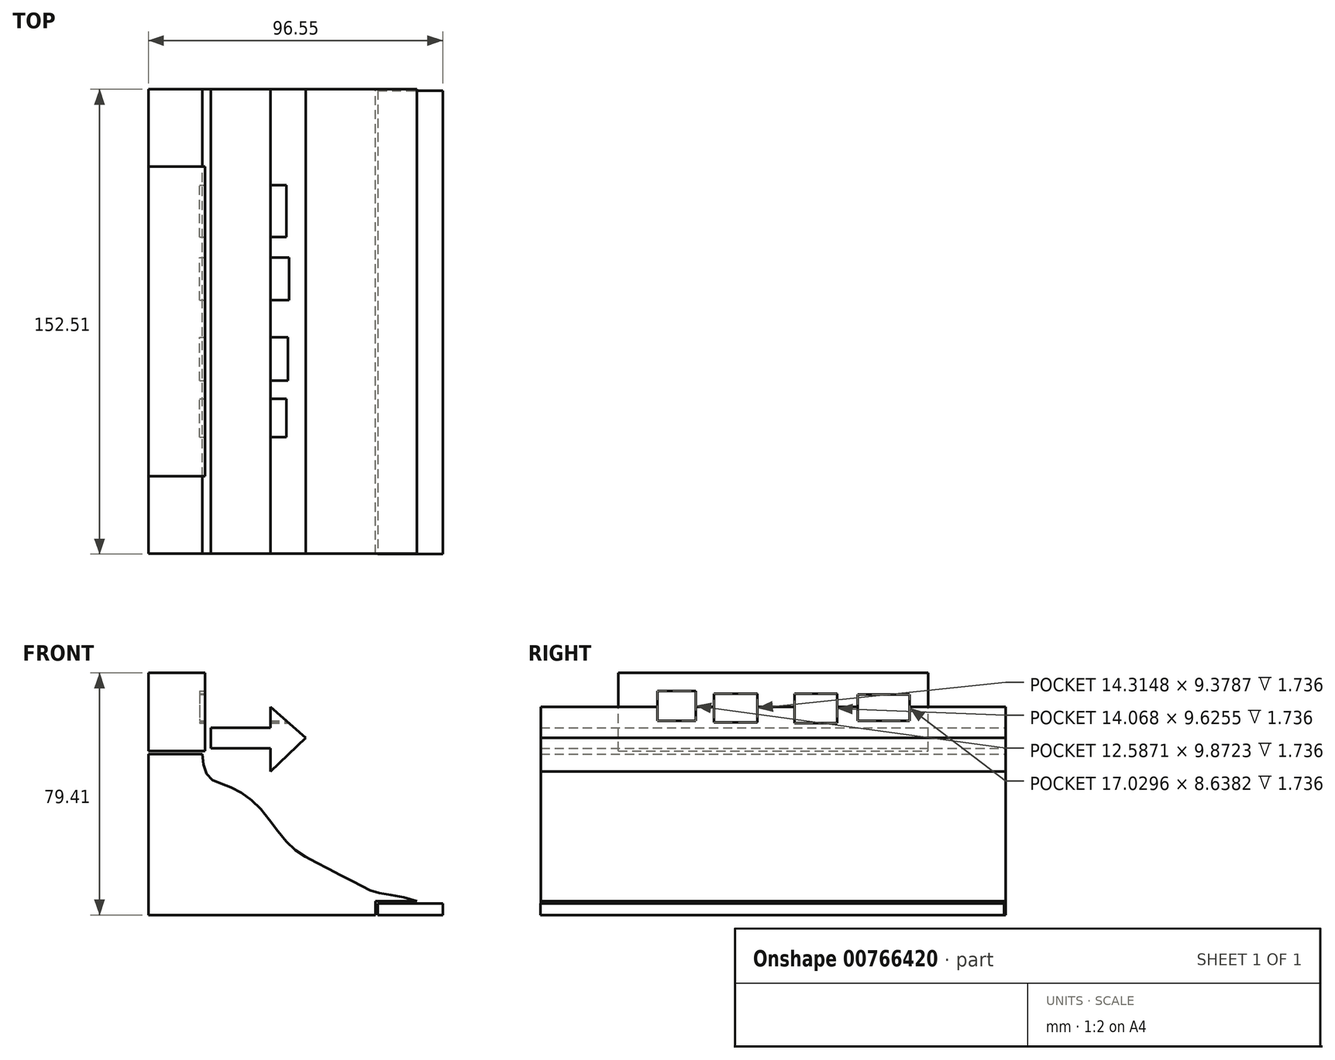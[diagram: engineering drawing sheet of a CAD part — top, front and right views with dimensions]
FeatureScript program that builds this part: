
annotation { "Feature Type Name" : "Feature", "Feature Type Description" : "" }
export const myFeature = defineFeature(function(context is Context, id is Id, definition is map)
    precondition{}
    {
        {
            var Q0;
            Q0=qCreatedBy(makeId("Top.planeOp"),FACE);
            var sketch = newSketch(context, id + "F0", { "sketchPlane" : qUnion([Q0])});
            skLineSegment(sketch, "E0.bottom", {"start": v(0, 75.77) * mm, "end": v(21.25, 75.77) * mm});
            skLineSegment(sketch, "E0.top", {"start": v(0, -76.3) * mm, "end": v(21.25, -76.3) * mm});
            skLineSegment(sketch, "E0.left", {"start": v(0, 75.77) * mm, "end": v(0, -76.3) * mm});
            skLineSegment(sketch, "E0.right", {"start": v(21.25, 75.77) * mm, "end": v(21.25, -76.3) * mm});
            skSolve(sketch);
        }
        {
            var Q0;
            Q0=qSketchRegion(id+"F0",true);
            extrude(context, id + "F1", {"entities" : qUnion([Q0]), "depth" : 3.8 * mm, "offsetDistance" : 25.4 * mm});
        }
        {
            var Q0;
            Q0=qCreatedBy(makeId("Front.planeOp"),FACE);
            var sketch = newSketch(context, id + "F2", { "sketchPlane" : qUnion([Q0])});
            skLineSegment(sketch, "E1", {"start": v(-75.3, 52.82) * mm, "end": v(-57.65, 52.82) * mm});
            skLineSegment(sketch, "E2", {"start": v(-75.3, 52.82) * mm, "end": v(-75.3, 0) * mm});
            skLineSegment(sketch, "E3", {"start": v(12.71, 4.49) * mm, "end": v(0, 4.49) * mm});
            skLineSegment(sketch, "E4", {"start": v(0, 4.49) * mm, "end": v(0, 0) * mm});
            skFitSpline(sketch, "E5", {"points": [v(-57.65, 52.82) * mm, v(-55.47, 45.32) * mm, v(-48.94, 42.17) * mm, v(-39.02, 35.4) * mm, v(-29.58, 23.54) * mm, v(-19.42, 16.77) * mm, v(-6.84, 10.24) * mm, v(0, 7.3) * mm, v(12.71, 4.49) * mm], "startDerivative": vector(9.74, -81.96) * mm, "endDerivative": vector(92.75, -41.23) * mm});
            skLineSegment(sketch, "E6.bottom", {"start": v(-54.78, 61.4) * mm, "end": v(-35.28, 61.4) * mm});
            skLineSegment(sketch, "E6.top", {"start": v(-54.78, 54.74) * mm, "end": v(-35.28, 54.74) * mm});
            skLineSegment(sketch, "E6.left", {"start": v(-54.78, 61.4) * mm, "end": v(-54.78, 54.74) * mm});
            skLineSegment(sketch, "E6.right", {"start": v(-35.28, 61.4) * mm, "end": v(-35.28, 54.74) * mm});
            skLineSegment(sketch, "E7", {"start": v(-35.28, 68.32) * mm, "end": v(-23.68, 58.07) * mm});
            skPoint(sketch, "E7.endSnap0", {"position": v(-35.28, 58.07) * mm});
            skLineSegment(sketch, "E8", {"start": v(-23.68, 58.07) * mm, "end": v(-35.28, 47.1) * mm});
            skLineSegment(sketch, "E9", {"start": v(-35.28, 47.1) * mm, "end": v(-35.28, 68.32) * mm});
            skLineSegment(sketch, "E10", {"start": v(-75.3, 0) * mm, "end": v(-0.85, 0) * mm});
            skLineSegment(sketch, "E11", {"start": v(-0.85, 0) * mm, "end": v(-0.85, 4.49) * mm});
            skLineSegment(sketch, "E12", {"start": v(-0.85, 4.49) * mm, "end": v(0, 4.49) * mm});
            skSolve(sketch);
        }
        {
            var Q0;
            Q0=makeQuery(id+"F2.imprint","IMPRINT",FACE,{"disambiguationData":[TD([[makeQuery(id+"F2.imprint","IMPRINT",EDGE,{"derivedFrom":sQuery(id+"F2.wireOp",EDGE,"E1")}),-1.0]])]});
            var Q1;
            {var subQ0=sQuery(id+"F2.wireOp",EDGE,"E6.bottom");Q1=makeQuery(id+"F2.imprint","IMPRINT",FACE,{"disambiguationData":[TD([[makeQuery(id+"F2.imprint","IMPRINT",EDGE,{"derivedFrom":subQ0}),-1.0]])]});}
            var Q2;
            {var subQ4=sQuery(id+"F2.wireOp",EDGE,"E7");Q2=makeQuery(id+"F2.imprint","IMPRINT",FACE,{"disambiguationData":[TD([[makeQuery(id+"F2.imprint","IMPRINT",EDGE,{"derivedFrom":subQ4}),-1.0]])]});}
            extrude(context, id + "F3", {"entities" : qUnion([Q0, Q1, Q2]), "operationType" : NewBodyOperationType.ADD, "depth" : 76.2 * mm, "offsetDistance" : 25.4 * mm});
        }
        {
            var Q0;
            Q0=makeQuery(id+"F3.opExtrude","CAP_FACE",FACE,{"disambiguationData":[OSD([sQuery(id+"F2.wireOp",EDGE,"E1"),sQuery(id+"F2.wireOp",EDGE,"4d570a10-8566-4800-adbc-9b14a9349e20"),sQuery(id+"F2.wireOp",EDGE,"E2"),sQuery(id+"F2.wireOp",EDGE,"zaHXE6N4-w8u5-yecR-uVTc-eUP8zXY4ykJm"),sQuery(id+"F2.wireOp",EDGE,"E3"),sQuery(id+"F2.wireOp",EDGE,"E4")])],"isStart":true});
            var Q1;
            Q1=makeQuery(id+"F3.opExtrude","CAP_FACE",FACE,{"disambiguationData":[OSD([sQuery(id+"F2.wireOp",EDGE,"E6.bottom"),sQuery(id+"F2.wireOp",EDGE,"E6.top"),sQuery(id+"F2.wireOp",EDGE,"E6.left"),sQuery(id+"F2.wireOp",EDGE,"E7"),sQuery(id+"F2.wireOp",EDGE,"E8"),sQuery(id+"F2.wireOp",EDGE,"E9")])],"isStart":true});
            extrude(context, id + "F4", {"entities" : qUnion([Q0, Q1]), "operationType" : NewBodyOperationType.ADD, "depth" : 76.2 * mm, "offsetDistance" : 25.4 * mm});
        }
        {
            var Q0;
            Q0=qCreatedBy(makeId("Front.planeOp"),FACE);
            var sketch = newSketch(context, id + "F5", { "sketchPlane" : qUnion([Q0])});
            skLineSegment(sketch, "E13.bottom", {"start": v(-75.3, 53.8) * mm, "end": v(-56.68, 53.8) * mm});
            skLineSegment(sketch, "E13.top", {"start": v(-75.3, 79.4) * mm, "end": v(-56.68, 79.4) * mm});
            skLineSegment(sketch, "E13.left", {"start": v(-75.3, 53.8) * mm, "end": v(-75.3, 79.4) * mm});
            skLineSegment(sketch, "E13.right", {"start": v(-56.68, 53.8) * mm, "end": v(-56.68, 79.4) * mm});
            skSolve(sketch);
        }
        {
            var Q0;
            Q0=makeQuery(id+"F5.imprint","IMPRINT",FACE,{"disambiguationData":[TD([[makeQuery(id+"F5.imprint","IMPRINT",EDGE,{"derivedFrom":sQuery(id+"F5.wireOp",EDGE,"E13.bottom")}),1.0]])]});
            extrude(context, id + "F6", {"entities" : qUnion([Q0]), "operationType" : NewBodyOperationType.ADD, "depth" : 50.8 * mm, "offsetDistance" : 25.4 * mm});
        }
        {
            var Q0;
            Q0=makeQuery(id+"F6.opExtrude","CAP_FACE",FACE,{"disambiguationData":[OSD([sQuery(id+"F5.wireOp",EDGE,"E13.bottom"),sQuery(id+"F5.wireOp",EDGE,"E13.top"),sQuery(id+"F5.wireOp",EDGE,"E13.left"),sQuery(id+"F5.wireOp",EDGE,"E13.right")])],"isStart":true});
            extrude(context, id + "F7", {"entities" : qUnion([Q0]), "operationType" : NewBodyOperationType.ADD, "depth" : 50.8 * mm, "offsetDistance" : 25.4 * mm});
        }
        {
            var Q0;
            Q0=qCreatedBy(makeId("Right.planeOp"),FACE);
            var sketch = newSketch(context, id + "F8", { "sketchPlane" : qUnion([Q0])});
            skLineSegment(sketch, "E14.bottom", {"start": v(-37.94, 73.55) * mm, "end": v(-25.35, 73.55) * mm});
            skLineSegment(sketch, "E14.top", {"start": v(-37.94, 63.67) * mm, "end": v(-25.35, 63.67) * mm});
            skLineSegment(sketch, "E14.left", {"start": v(-37.94, 73.55) * mm, "end": v(-37.94, 63.67) * mm});
            skLineSegment(sketch, "E14.right", {"start": v(-25.35, 73.55) * mm, "end": v(-25.35, 63.67) * mm});
            skLineSegment(sketch, "E15.bottom", {"start": v(-19.43, 72.56) * mm, "end": v(-5.11, 72.56) * mm});
            skLineSegment(sketch, "E15.top", {"start": v(-19.43, 63.18) * mm, "end": v(-5.11, 63.18) * mm});
            skLineSegment(sketch, "E15.left", {"start": v(-19.43, 72.56) * mm, "end": v(-19.43, 63.18) * mm});
            skLineSegment(sketch, "E15.right", {"start": v(-5.11, 72.56) * mm, "end": v(-5.11, 63.18) * mm});
            skLineSegment(sketch, "E16.bottom", {"start": v(6.98, 72.56) * mm, "end": v(21.05, 72.56) * mm});
            skLineSegment(sketch, "E16.top", {"start": v(6.98, 62.93) * mm, "end": v(21.05, 62.93) * mm});
            skLineSegment(sketch, "E16.left", {"start": v(6.98, 72.56) * mm, "end": v(6.98, 62.93) * mm});
            skLineSegment(sketch, "E16.right", {"start": v(21.05, 72.56) * mm, "end": v(21.05, 62.93) * mm});
            skLineSegment(sketch, "E17.bottom", {"start": v(27.71, 72.31) * mm, "end": v(44.74, 72.31) * mm});
            skLineSegment(sketch, "E17.top", {"start": v(27.71, 63.67) * mm, "end": v(44.74, 63.67) * mm});
            skLineSegment(sketch, "E17.left", {"start": v(27.71, 72.31) * mm, "end": v(27.71, 63.67) * mm});
            skLineSegment(sketch, "E17.right", {"start": v(44.74, 72.31) * mm, "end": v(44.74, 63.67) * mm});
            skSolve(sketch);
        }
        {
            var Q0;
            Q0=makeQuery(id+"F8.imprint","IMPRINT",FACE,{"disambiguationData":[TD([[makeQuery(id+"F8.imprint","IMPRINT",EDGE,{"derivedFrom":sQuery(id+"F8.wireOp",EDGE,"E15.bottom")}),-1.0]])]});
            var Q1;
            Q1=makeQuery(id+"F8.imprint","IMPRINT",FACE,{"disambiguationData":[TD([[makeQuery(id+"F8.imprint","IMPRINT",EDGE,{"derivedFrom":sQuery(id+"F8.wireOp",EDGE,"E16.bottom")}),-1.0]])]});
            var Q2;
            Q2=makeQuery(id+"F8.imprint","IMPRINT",FACE,{"disambiguationData":[TD([[makeQuery(id+"F8.imprint","IMPRINT",EDGE,{"derivedFrom":sQuery(id+"F8.wireOp",EDGE,"E14.bottom")}),-1.0]])]});
            var Q3;
            Q3=makeQuery(id+"F8.imprint","IMPRINT",FACE,{"disambiguationData":[TD([[makeQuery(id+"F8.imprint","IMPRINT",EDGE,{"derivedFrom":sQuery(id+"F8.wireOp",EDGE,"E17.bottom")}),-1.0]])]});
            extrude(context, id + "F9", {"entities" : qUnion([Q0, Q1, Q2, Q3]), "operationType" : NewBodyOperationType.REMOVE, "oppositeDirection" : true, "depth" : 58.42 * mm, "offsetDistance" : 25.4 * mm});
        }
    });
